# Revit family: Tief-Kühltische GN1-1 - Eigen
name_source: partatom
category: Sonderausstattung
revit_build: Autodesk Revit 2015 (Build: 20160512_1515(x64)
units: mm (PartAtom-declared; Revit-internal decimal feet)

## types (15) — shared parameters
Abstand Display seitlich = 60 mm  [stored 0.19685 ft]
Aufkantung Höhe = 50 mm  [stored 0.164042 ft]
Aufkantung Stärke = 6 mm  [stored 0.019685 ft]
Höhe Elektroanschluss = 150 mm  [stored 0.492126 ft]
Korpus Tiefe = 620 mm
Kältemittel = R134a
Material = Edelstahl AISI 304
Pfosten Breite = 100 mm  [stored 0.328084 ft]
Pfosten Tiefe = 50 mm  [stored 0.164042 ft]
Platte Stärke = 50 mm  [stored 0.164042 ft]
Platte Tiefe = 700 mm  [stored 2.29659 ft]
Rückwand Stärke = 50 mm  [stored 0.164042 ft]
Scheinleistung = 0 VA
Seitenteilwand Stärke = 15 mm  [stored 0.0492126 ft]
Seitenwand Stärke = 50 mm  [stored 0.164042 ft]
Sockelhöhe = 150 mm  [stored 0.492126 ft]
Spannung = 230 V
Temp. Bereich = -18°C bis -20°C
Tür_1 = Ja
Türen Stärke = 50 mm  [stored 0.164042 ft]
Wand oben Stärke = 50 mm  [stored 0.164042 ft]
Wand unten Stärke = 50 mm  [stored 0.164042 ft]
Öffnungstiefe = 470 mm

## per-type parameters (varying)
| type | Abstand Logo | Artnr mit Platte | Artnr mit Platte und Aufkantung | Artnr ohne Platte | Breite | Energieverbrauch | Kapazität | Korpus Breite | Korpus Höhe | Kälteleistung | Pfosten 1 | Pfosten 2 | Pfosten Abstand | Pfosten Anzahl | Seitenteil Breite | Tür_2 | Tür_3 | Türen Anzahl | Türen Breite | Türen Breite halb | Türen Höhe | Türen Lücke | Versatz Tür zu Seitenteil | Watt |
| 650x790 1-türig | 265 mm | TKM 711162 | TKM 711161 | TKM 711160 | 790 mm  [stored 2.59186 ft] | 7,1 kWh/24 h | 1 x 7 x GN1/1 | 445 mm  [stored 1.45997 ft] | 650 mm  [stored 2.13255 ft] | 250 Watt -30°C VT/+32°C UT | Nein | Nein | 400 mm  [stored 1.31234 ft] | 0 | 330 mm | Nein | Nein | 1 | 390 mm  [stored 1.27953 ft] | 195 mm  [stored 0.639764 ft] | 630 mm  [stored 2.06693 ft] | 20 mm  [stored 0.0656168 ft] | 40 mm  [stored 0.131234 ft] | 650 W |
| 650x1250 2-türig | 265 mm | TKM 721162 | TKM 721161 | TKM 721160 | 1250 mm  [stored 4.10105 ft] | 7,7 kWh/24 h | 2 x 9 x GN1/1 | 915 mm  [stored 3.00197 ft] | 650 mm  [stored 2.13255 ft] | 250 Watt -30°C VT/+32°C UT | Ja | Nein | 440 mm | 1 | 320 mm  [stored 1.04987 ft] | Ja | Nein | 2 | 430 mm  [stored 1.41076 ft] | 215 mm  [stored 0.705381 ft] | 630 mm  [stored 2.06693 ft] | 20 mm  [stored 0.0656168 ft] | 20 mm  [stored 0.0656168 ft] | 680 W |
| 650x1725 3-türig | 265 mm | TKM 731162 | TKM 731161 | TKM 731160 | 1725 mm  [stored 5.65945 ft] | 8,3 kWh/24 h | 3 x 9 x GN1/1 | 1390 mm  [stored 4.56037 ft] | 650 mm  [stored 2.13255 ft] | 460 Watt -30°C VT/+32°C UT | Ja | Ja | 445 mm  [stored 1.45997 ft] | 2 | 320 mm  [stored 1.04987 ft] | Ja | Ja | 3 | 430 mm  [stored 1.41076 ft] | 215 mm  [stored 0.705381 ft] | 630 mm  [stored 2.06693 ft] | 30 mm  [stored 0.0984252 ft] | 25 mm  [stored 0.082021 ft] | 750 W |
| 700x790 1-türig | 290 mm | TKM 711172-70 | TKM 711171-70 | TKM 711170-70 | 790 mm  [stored 2.59186 ft] | 7,1 kWh/24 h | 1 x 8 x GN1/1 | 445 mm  [stored 1.45997 ft] | 700 mm  [stored 2.29659 ft] | 250 Watt -30°C VT/+32°C UT | Nein | Nein | 400 mm  [stored 1.31234 ft] | 0 | 330 mm | Nein | Nein | 1 | 390 mm  [stored 1.27953 ft] | 195 mm  [stored 0.639764 ft] | 680 mm  [stored 2.23097 ft] | 20 mm  [stored 0.0656168 ft] | 40 mm  [stored 0.131234 ft] | 650 W |
| 700x1250 2-türig | 290 mm | TKM 721172-70 | TKM 721171-70 | TKM 721170-70 | 1250 mm  [stored 4.10105 ft] | 7,7 kWh/24 h | 2 x 10 x GN1/1 | 915 mm  [stored 3.00197 ft] | 700 mm  [stored 2.29659 ft] | 250 Watt -30°C VT/+32°C UT | Ja | Nein | 440 mm | 1 | 320 mm  [stored 1.04987 ft] | Ja | Nein | 2 | 430 mm  [stored 1.41076 ft] | 215 mm  [stored 0.705381 ft] | 680 mm  [stored 2.23097 ft] | 20 mm  [stored 0.0656168 ft] | 20 mm  [stored 0.0656168 ft] | 680 W |
| 700x1725 3-türig | 290 mm | TKM 731172-70 | TKM 731171-70 | TKM 731170-70 | 1725 mm  [stored 5.65945 ft] | 8,3 kWh/24 h | 3 x 10 x GN1/1 | 1390 mm  [stored 4.56037 ft] | 700 mm  [stored 2.29659 ft] | 460 Watt -30°C VT/+32°C UT | Ja | Ja | 445 mm  [stored 1.45997 ft] | 2 | 320 mm  [stored 1.04987 ft] | Ja | Ja | 3 | 430 mm  [stored 1.41076 ft] | 215 mm  [stored 0.705381 ft] | 680 mm  [stored 2.23097 ft] | 30 mm  [stored 0.0984252 ft] | 25 mm  [stored 0.082021 ft] | 750 W |
| 710x790 1-türig | 295 mm  [stored 0.967848 ft] | TKM 711171-71 |  | TKM 711170-71 | 790 mm  [stored 2.59186 ft] |  | 1 x 8 x GN1/1 | 445 mm  [stored 1.45997 ft] | 710 mm | 250 Watt -30°C VT/+32°C UT | Nein | Nein | 400 mm  [stored 1.31234 ft] | 0 | 330 mm | Nein | Nein | 1 | 390 mm  [stored 1.27953 ft] | 195 mm  [stored 0.639764 ft] | 690 mm  [stored 2.26378 ft] | 20 mm  [stored 0.0656168 ft] | 40 mm  [stored 0.131234 ft] | 650 W |
| 710x1250 2-türig | 295 mm  [stored 0.967848 ft] | TKM 721171-71 |  | TKM 721170-71 | 1250 mm  [stored 4.10105 ft] | 7,7 kWh/24 h | 2 x 10 x GN1/1 | 915 mm  [stored 3.00197 ft] | 710 mm | 250 Watt -30°C VT/+32°C UT | Ja | Nein | 440 mm | 1 | 320 mm  [stored 1.04987 ft] | Ja | Nein | 2 | 430 mm  [stored 1.41076 ft] | 215 mm  [stored 0.705381 ft] | 690 mm  [stored 2.26378 ft] | 20 mm  [stored 0.0656168 ft] | 20 mm  [stored 0.0656168 ft] | 680 W |
| 710x1725 3-türig | 295 mm  [stored 0.967848 ft] | TKM 731171-71 |  | TKM 731170-71 | 1725 mm  [stored 5.65945 ft] | 8,3 kWh/24 h | 3 x 10 x GN1/1 | 1390 mm  [stored 4.56037 ft] | 710 mm | 460 Watt -30°C VT/+32°C UT | Ja | Ja | 445 mm  [stored 1.45997 ft] | 2 | 320 mm  [stored 1.04987 ft] | Ja | Ja | 3 | 430 mm  [stored 1.41076 ft] | 215 mm  [stored 0.705381 ft] | 690 mm  [stored 2.26378 ft] | 30 mm  [stored 0.0984252 ft] | 25 mm  [stored 0.082021 ft] | 750 W |
| 750x790 1-türig | 315 mm  [stored 1.03346 ft] | TKM 711172 | TKM 711171 | TKM 711170 | 790 mm  [stored 2.59186 ft] | 7,2 kWh/24 h | 1 x 9 x GN1/1 | 445 mm  [stored 1.45997 ft] | 750 mm  [stored 2.46063 ft] | 250 Watt -30°C VT/+32°C UT | Nein | Nein | 400 mm  [stored 1.31234 ft] | 0 | 330 mm | Nein | Nein | 1 | 390 mm  [stored 1.27953 ft] | 195 mm  [stored 0.639764 ft] | 730 mm  [stored 2.39501 ft] | 20 mm  [stored 0.0656168 ft] | 40 mm  [stored 0.131234 ft] | 650 W |
| 750x1725 3-türig | 315 mm  [stored 1.03346 ft] | TKM 731172 | TKM 731171 | TKM 731170 | 1725 mm  [stored 5.65945 ft] | 8,4 kWh/24 h | 3 x 11 x GN1/1 | 1390 mm  [stored 4.56037 ft] | 750 mm  [stored 2.46063 ft] | 460 Watt -30°C VT/+32°C UT | Ja | Ja | 445 mm  [stored 1.45997 ft] | 2 | 320 mm  [stored 1.04987 ft] | Ja | Ja | 3 | 430 mm  [stored 1.41076 ft] | 215 mm  [stored 0.705381 ft] | 730 mm  [stored 2.39501 ft] | 30 mm  [stored 0.0984252 ft] | 25 mm  [stored 0.082021 ft] | 750 W |
| 750x1250 2-türig | 315 mm  [stored 1.03346 ft] | TKM 721172 | TKM 721171 | TKM 721170 | 1250 mm  [stored 4.10105 ft] | 7,8 kWh/24 h | 2 x 11 x GN1/1 | 915 mm  [stored 3.00197 ft] | 750 mm  [stored 2.46063 ft] | 250 Watt -30°C VT/+32°C UT | Ja | Nein | 440 mm | 1 | 320 mm  [stored 1.04987 ft] | Ja | Nein | 2 | 430 mm  [stored 1.41076 ft] | 215 mm  [stored 0.705381 ft] | 730 mm  [stored 2.39501 ft] | 20 mm  [stored 0.0656168 ft] | 20 mm  [stored 0.0656168 ft] | 680 W |
| 760x790 1-türig | 320 mm  [stored 1.04987 ft] | TKM 711171-76 |  | TKM 711170-76 | 790 mm  [stored 2.59186 ft] | 7,2 kWh/24 h | 1 x 9 x GN1/1 | 445 mm  [stored 1.45997 ft] | 760 mm | 250 Watt -30°C VT/+32°C UT | Nein | Nein | 400 mm  [stored 1.31234 ft] | 0 | 330 mm | Nein | Nein | 1 | 390 mm  [stored 1.27953 ft] | 195 mm  [stored 0.639764 ft] | 740 mm  [stored 2.42782 ft] | 20 mm  [stored 0.0656168 ft] | 40 mm  [stored 0.131234 ft] | 650 W |
| 760x1250 2-türig | 320 mm  [stored 1.04987 ft] | TKM 721171-76 |  | TKM 721170-76 | 1250 mm  [stored 4.10105 ft] | 7,8 kWh/24 h | 2 x 11 x GN1/1 | 915 mm  [stored 3.00197 ft] | 760 mm | 250 Watt -30°C VT/+32°C UT | Ja | Nein | 440 mm | 1 | 320 mm  [stored 1.04987 ft] | Ja | Nein | 2 | 430 mm  [stored 1.41076 ft] | 215 mm  [stored 0.705381 ft] | 740 mm  [stored 2.42782 ft] | 20 mm  [stored 0.0656168 ft] | 20 mm  [stored 0.0656168 ft] | 680 W |
| 760x1725 3-türig | 320 mm  [stored 1.04987 ft] | TKM 731171-76 |  | TKM 731170-76 | 1725 mm  [stored 5.65945 ft] | 8,4 kWh/24 h | 3 x 11 x GN1/1 | 1390 mm  [stored 4.56037 ft] | 760 mm | 460 Watt -30°C VT/+32°C UT | Ja | Ja | 445 mm  [stored 1.45997 ft] | 2 | 320 mm  [stored 1.04987 ft] | Ja | Ja | 3 | 430 mm  [stored 1.41076 ft] | 215 mm  [stored 0.705381 ft] | 740 mm  [stored 2.42782 ft] | 30 mm  [stored 0.0984252 ft] | 25 mm  [stored 0.082021 ft] | 750 W |

note: [stored X ft] marks values corroborated as IEEE doubles in the binary element streams (Revit-internal decimal feet)

## geometry (parser evidence)
native form markers: Blend x15, Sweep x2
no freeform markers — native parametric forms only
